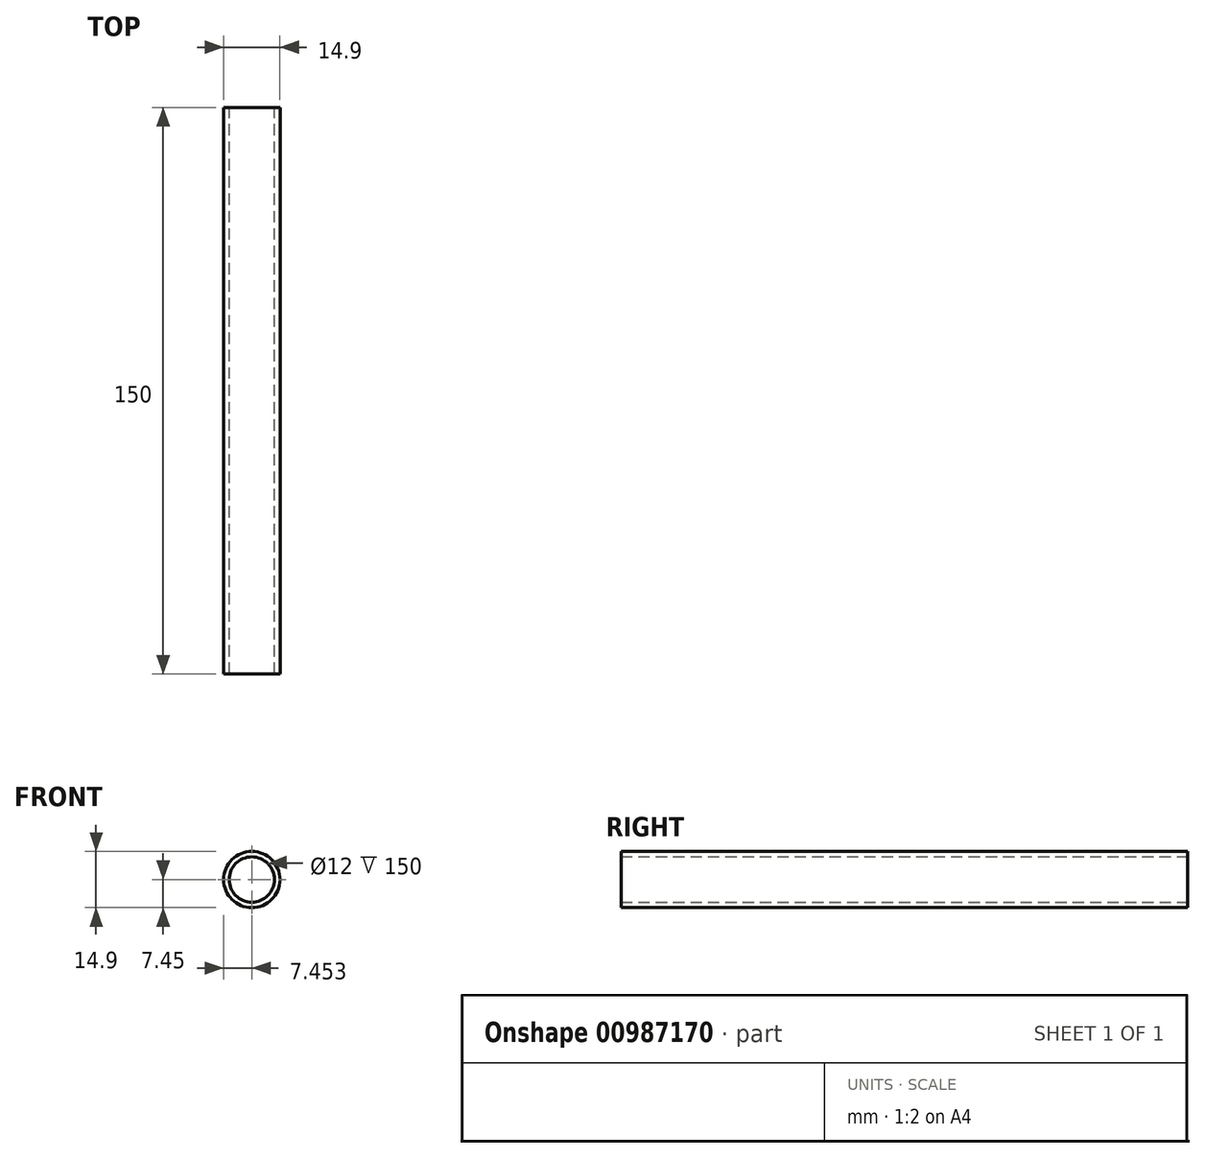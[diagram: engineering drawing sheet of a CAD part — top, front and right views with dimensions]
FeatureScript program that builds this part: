
annotation { "Feature Type Name" : "Feature", "Feature Type Description" : "" }
export const myFeature = defineFeature(function(context is Context, id is Id, definition is map)
    precondition{}
    {
        {
            var Q0;
            Q0=qCreatedBy(makeId("Front.planeOp"),FACE);
            var sketch = newSketch(context, id + "F0", { "sketchPlane" : qUnion([Q0])});
            skCircle(sketch, "E0", {"center": v(-52.75, 0) * mm, "radius": 7.45 * mm});
            skCircle(sketch, "E1", {"center": v(-52.75, 0) * mm, "radius": 6 * mm});
            skSolve(sketch);
        }
        {
            var Q0;
            Q0=makeQuery(id+"F0.imprint","IMPRINT",FACE,{"disambiguationData":[TD([[makeQuery(id+"F0.imprint","IMPRINT",EDGE,{"derivedFrom":sQuery(id+"F0.wireOp",EDGE,"E0")}),1.0]])]});
            var Q1;
            Q1=sQuery(id+"F0.wireOp",EDGE,"E0");
            extrude(context, id + "F1", {"entities" : qUnion([Q0]), "surfaceEntities" : qUnion([Q1]), "depth" : 150 * mm, "offsetDistance" : 25 * mm});
        }
    });
